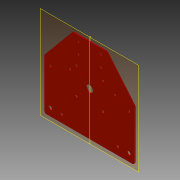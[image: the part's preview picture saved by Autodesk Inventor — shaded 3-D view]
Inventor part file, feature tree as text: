
AUTODESK INVENTOR PART (.ipt)
format: ipt  version: 2013 (Build 170138000, 138)  size: 193,024 bytes
history: native  units: in
note: dims shown in document units (in); Inventor stores cm internally (conversion verified against a paired STEP export)
features: extrude x7, sketch x7, pattern_linear x2, plane x2, fillet x1, mirror x1
ambient origin geometry x8: Origin, YZ Plane, XZ Plane, XY Plane, X Axis, Y Axis, Z Axis, Center Point
bodies: Solid1 (feature_tree)
feature tree (20):
  extrude  "Extrusion1"  Depth=2.3622in
  extrude  "Extrusion2"  Depth=3.5433in
  pattern_linear  "Rectangular Pattern1"  Count1=9  [1 undecoded]
  extrude  "Extrusion3"  Depth=0.0747in TaperAngle=0.0deg
  extrude  "Extrusion4"  Depth=0.5in
  extrude  "Extrusion5"  Depth=0.3937in
  extrude  "Extrusion6"  Depth=0.1969in
  pattern_linear  "Rectangular Pattern2"  Count1=2  [1 undecoded]
  fillet  "Fillet2"  Radius=0.5118in
  extrude  "Extrusion7"  Depth=3.1496in
  plane  "Work Plane1"
  plane  "Work Plane2"
  mirror  "Mirror1"
  sketch  "Sketch1"  dims[d0=6.2992in d4=2.3622in]
  sketch  "Sketch2"  dims[d5=1.9685in d6=3.5433in d7=3.5433in]
  sketch  "Sketch3"  dims[d8=5.9055in d9=0.0747in d10=0.0in]
  sketch  "Sketch4"  dims[d11=0.281in d12=0.5in]
  sketch  "Sketch5"  dims[d13=0.3937in d14=0.3937in]
  sketch  "Sketch6"  dims[d15=2.5433in d16=0.1969in]
  sketch  "Sketch7"  dims[d17=0.1345in d18=0.0in d19=0.7874in d21=5.5118in d22=0.5118in d23=3.1496in d24=3.0433in d25=0.1345in d26=0.0in d27=0.1181in d28=2.4333in d29=2.5396in d30=0.1181in d31=2.4333in d32=3.7596in d33=0.1181in d34=0.1181in d35=2.5396in d36=3.6533in d37=3.6533in d38=3.7596in d39=1.7717in d40=0.5in d41=0.1969in d42=1.378in d43=0.5in d44=0.1969in d45=0.1345in d46=0.0in d47=0.3937in d48=0.3937in d49=0.7874in d50=0.3937in d51=0.1969in d52=0.1969in d53=0.1345in d54=0.0in d55=2.22in d56=2.113in d57=0.2in d58=0.1345in d59=0.0in d60=0.7874in d62=1.86in d63=0.7874in d65=1.86in d67=0.125in d68=0.1969in d69=0.5in d70=1.1811in d71=0.1969in d72=1.1811in d73=0.5in d74=1.0in d75=0.0in]
note: 2 required parameter values undecoded (feature->parameter linkage not recoverable at this tier; creation-order binding heuristic only, values carry confidence <= 0.55)
